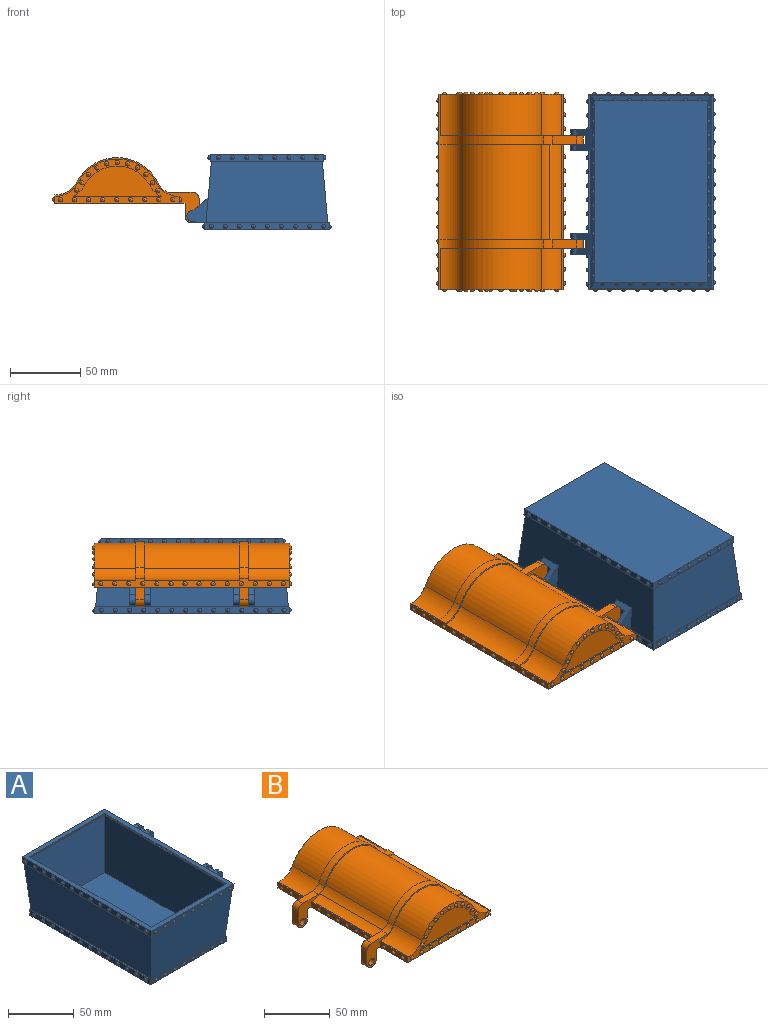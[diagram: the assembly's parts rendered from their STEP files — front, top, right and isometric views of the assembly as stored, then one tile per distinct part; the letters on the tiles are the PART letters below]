
ASSEMBLY  parts=2 mates=1
PART A: 134 faces, bbox 102.8x141.6x54 mm
  f0: plane 15x9.96mm, normal (0.09,0,1), area 101mm2, adj f11,f30,f31,f35,f36,f37,f40,f41
  f1: plane 15x9.96mm, normal (0.09,0,1), area 101mm2, adj f11,f28,f29,f32,f33,f34,f42,f43
  f2: plane 86.7x44mm, normal (0,-1,-0.09), area 3659.3mm2, adj f5,f9,f10,f11
  f3: plane 139x88.7mm, normal (0,0,1), area 1760.1mm2, adj f4,f12,f14,f17,f22,f25,f26,f27
  f4: plane 139x5mm, normal (-1,0,0), area 593.9mm2, adj f3,f11,f14,f17,f76,f77,f78,f79
  f5: plane 137.13x44mm, normal (-1,0,-0.09), area 5886.5mm2, adj f2,f9,f11,f13
  f6: plane 130.43x5mm, normal (-1,0,0), area 558.1mm2, adj f7,f9,f15,f16,f90,f91,f92,f93
  f7: plane 129.55x81mm, normal (0,0,-1), area 10493.6mm2, adj f6,f8,f15,f16
  f8: plane 130.43x5mm, normal (1,0,0), area 558.1mm2, adj f7,f9,f15,f16,f111,f112,f113,f114
  f9: plane 130.43x81mm, normal (0,0,1), area 339.9mm2, adj f2,f5,f6,f8,f10,f13,f15,f16
  f10: plane 137.13x44mm, normal (1,0,-0.09), area 5346.5mm2, adj f2,f9,f11,f13,f28,f29,f30,f31
  f11: plane 138.13x88.7mm, normal (0,0,-1), area 362.9mm2, adj f0,f1,f2,f4,f5,f10,f12,f13
  f12: plane 139x5mm, normal (1,0,0), area 593.9mm2, adj f3,f11,f14,f17,f53,f54,f55,f56
  f13: plane 86.7x44mm, normal (0,1,-0.09), area 3659.3mm2, adj f5,f9,f10,f11
  f14: plane 88.7x5mm, normal (0,-1,-0.09), area 381.6mm2, adj f3,f4,f11,f12,f44,f45,f46,f47
  f15: plane 81x5mm, normal (0,-1,-0.09), area 350mm2, adj f6,f7,f8,f9,f124,f125,f126,f127
  f16: plane 81x5mm, normal (0,1,-0.09), area 350mm2, adj f6,f7,f8,f9,f103,f104,f105,f106
  f17: plane 88.7x5mm, normal (0,1,-0.09), area 381.6mm2, adj f3,f4,f11,f12,f67,f68,f69,f70
  f18: plane 129.79x49mm, normal (1,0,0.09), area 6173.4mm2, adj f19,f21,f23,f24
  f19: plane 79.37x49mm, normal (0,1,0.09), area 3693mm2, adj f18,f20,f23,f24
  f20: plane 129.79x49mm, normal (-1,0,0.09), area 6173.4mm2, adj f19,f21,f23,f24
  f21: plane 79.37x49mm, normal (0,-1,0.09), area 3693mm2, adj f18,f20,f23,f24
  f22: plane 130.97x1mm, normal (1,0,0), area 130.9mm2, adj f3,f24,f26,f27
  f23: plane 121.22x70.79mm, normal (0,0,1), area 8581.7mm2, adj f18,f19,f20,f21
  f24: plane 130.79x80.7mm, normal (0,0,1), area 253.4mm2, adj f18,f19,f20,f21,f22,f25,f26,f27
  f25: plane 130.97x1mm, normal (-1,0,0), area 130.9mm2, adj f3,f24,f26,f27
  f26: plane 80.7x1mm, normal (0,1,0.09), area 81mm2, adj f3,f22,f24,f25
  f27: plane 80.7x1mm, normal (0,-1,0.09), area 81mm2, adj f3,f22,f24,f25
  f28: plane 17.93x15.18mm, normal (0,-1,0), area 155.1mm2, adj f1,f10,f43,f133
  f29: plane 17.93x15.18mm, normal (0,1,0), area 155.1mm2, adj f1,f10,f42,f133
  f30: plane 17.93x15.18mm, normal (0,1,0), area 155.1mm2, adj f0,f10,f40,f132
  f31: plane 17.93x15.18mm, normal (0,-1,0), area 155.1mm2, adj f0,f10,f41,f132
  f32: plane 14.94x11.93mm, normal (0,1,0), area 93.1mm2, adj f1,f34,f38,f43,f133
  f33: plane 14.94x11.93mm, normal (0,-1,0), area 93.1mm2, adj f1,f34,f38,f42,f133
  f34: plane 14.94x7mm, normal (1,0,-0.09), area 105mm2, adj f1,f32,f33,f133
  f35: plane 14.94x11.93mm, normal (0,1,0), area 93.1mm2, adj f0,f37,f39,f41,f132
  f36: plane 14.94x11.93mm, normal (0,-1,0), area 93.1mm2, adj f0,f37,f39,f40,f132
  f37: plane 14.94x7mm, normal (1,0,-0.09), area 105mm2, adj f0,f35,f36,f132
  f38: cylinder r=2mm len=7mm, axis (0,-1,0), area 88mm2, adj f32,f33
  f39: cylinder r=2mm len=7mm, axis (0,1,0), area 88mm2, adj f35,f36
  f40: cylinder r=4mm len=7.98mm, axis (0,-1,0), area 50.3mm2, adj f0,f30,f36,f132
  f41: cylinder r=4mm len=7.98mm, axis (0,1,0), area 50.3mm2, adj f0,f31,f35,f132
  f42: cylinder r=4mm len=7.98mm, axis (0,-1,0), area 50.3mm2, adj f1,f29,f33,f133
  f43: cylinder r=4mm len=7.98mm, axis (0,1,0), area 50.3mm2, adj f1,f28,f32,f133
  f44: sphere r=1.5mm, area 14.1mm2, adj f14
  f45: sphere r=1.5mm, area 14.1mm2, adj f14
  f46: sphere r=1.5mm, area 14.1mm2, adj f14
  f47: sphere r=1.5mm, area 14.1mm2, adj f14
  f48: sphere r=1.5mm, area 14.1mm2, adj f14
  f49: sphere r=1.5mm, area 14.1mm2, adj f14
  f50: sphere r=1.5mm, area 14.1mm2, adj f14
  f51: sphere r=1.5mm, area 14.1mm2, adj f14
  f52: sphere r=1.5mm, area 14.1mm2, adj f14
  f53: sphere r=1.5mm, area 14.1mm2, adj f12
  f54: sphere r=1.5mm, area 14.1mm2, adj f12
  f55: sphere r=1.5mm, area 14.1mm2, adj f12
  f56: sphere r=1.5mm, area 14.1mm2, adj f12
  f57: sphere r=1.5mm, area 14.1mm2, adj f12
  f58: sphere r=1.5mm, area 14.1mm2, adj f12
  f59: sphere r=1.5mm, area 14.1mm2, adj f12
  f60: sphere r=1.5mm, area 14.1mm2, adj f12
  f61: sphere r=1.5mm, area 14.1mm2, adj f12
  f62: sphere r=1.5mm, area 14.1mm2, adj f12
  f63: sphere r=1.5mm, area 14.1mm2, adj f12
  f64: sphere r=1.5mm, area 14.1mm2, adj f12
  f65: sphere r=1.5mm, area 14.1mm2, adj f12
  f66: sphere r=1.5mm, area 14.1mm2, adj f12
  f67: sphere r=1.5mm, area 14.1mm2, adj f17
  f68: sphere r=1.5mm, area 14.1mm2, adj f17
  f69: sphere r=1.5mm, area 14.1mm2, adj f17
  f70: sphere r=1.5mm, area 14.1mm2, adj f17
  f71: sphere r=1.5mm, area 14.1mm2, adj f17
  f72: sphere r=1.5mm, area 14.1mm2, adj f17
  f73: sphere r=1.5mm, area 14.1mm2, adj f17
  f74: sphere r=1.5mm, area 14.1mm2, adj f17
  f75: sphere r=1.5mm, area 14.1mm2, adj f17
  f76: sphere r=1.5mm, area 14.1mm2, adj f4
  f77: sphere r=1.5mm, area 14.1mm2, adj f4
  f78: sphere r=1.5mm, area 14.1mm2, adj f4
  f79: sphere r=1.5mm, area 14.1mm2, adj f4
  f80: sphere r=1.5mm, area 14.1mm2, adj f4
  f81: sphere r=1.5mm, area 14.1mm2, adj f4
  f82: sphere r=1.5mm, area 14.1mm2, adj f4
  f83: sphere r=1.5mm, area 14.1mm2, adj f4
  f84: sphere r=1.5mm, area 14.1mm2, adj f4
  f85: sphere r=1.5mm, area 14.1mm2, adj f4
  f86: sphere r=1.5mm, area 14.1mm2, adj f4
  f87: sphere r=1.5mm, area 14.1mm2, adj f4
  f88: sphere r=1.5mm, area 14.1mm2, adj f4
  f89: sphere r=1.5mm, area 14.1mm2, adj f4
  f90: sphere r=1.5mm, area 14.1mm2, adj f6
  f91: sphere r=1.5mm, area 14.1mm2, adj f6
  f92: sphere r=1.5mm, area 14.1mm2, adj f6
  f93: sphere r=1.5mm, area 14.1mm2, adj f6
  f94: sphere r=1.5mm, area 14.1mm2, adj f6
  f95: sphere r=1.5mm, area 14.1mm2, adj f6
  f96: sphere r=1.5mm, area 14.1mm2, adj f6
  f97: sphere r=1.5mm, area 14.1mm2, adj f6
  f98: sphere r=1.5mm, area 14.1mm2, adj f6
  f99: sphere r=1.5mm, area 14.1mm2, adj f6
  f100: sphere r=1.5mm, area 14.1mm2, adj f6
  f101: sphere r=1.5mm, area 14.1mm2, adj f6
  f102: sphere r=1.5mm, area 14.1mm2, adj f6
  f103: sphere r=1.5mm, area 14.1mm2, adj f16
  f104: sphere r=1.5mm, area 14.1mm2, adj f16
  f105: sphere r=1.5mm, area 14.1mm2, adj f16
  f106: sphere r=1.5mm, area 14.1mm2, adj f16
  f107: sphere r=1.5mm, area 14.1mm2, adj f16
  f108: sphere r=1.5mm, area 14.1mm2, adj f16
  f109: sphere r=1.5mm, area 14.1mm2, adj f16
  f110: sphere r=1.5mm, area 14.1mm2, adj f16
  f111: sphere r=1.5mm, area 14.1mm2, adj f8
  f112: sphere r=1.5mm, area 14.1mm2, adj f8
  f113: sphere r=1.5mm, area 14.1mm2, adj f8
  f114: sphere r=1.5mm, area 14.1mm2, adj f8
  f115: sphere r=1.5mm, area 14.1mm2, adj f8
  f116: sphere r=1.5mm, area 14.1mm2, adj f8
  f117: sphere r=1.5mm, area 14.1mm2, adj f8
  f118: sphere r=1.5mm, area 14.1mm2, adj f8
  f119: sphere r=1.5mm, area 14.1mm2, adj f8
  f120: sphere r=1.5mm, area 14.1mm2, adj f8
  f121: sphere r=1.5mm, area 14.1mm2, adj f8
  f122: sphere r=1.5mm, area 14.1mm2, adj f8
  f123: sphere r=1.5mm, area 14.1mm2, adj f8
  f124: sphere r=1.5mm, area 14.1mm2, adj f15
  f125: sphere r=1.5mm, area 14.1mm2, adj f15
  f126: sphere r=1.5mm, area 14.1mm2, adj f15
  f127: sphere r=1.5mm, area 14.1mm2, adj f15
  f128: sphere r=1.5mm, area 14.1mm2, adj f15
  f129: sphere r=1.5mm, area 14.1mm2, adj f15
  f130: sphere r=1.5mm, area 14.1mm2, adj f15
  f131: sphere r=1.5mm, area 14.1mm2, adj f15
  f132: plane 15x10.83mm, normal (0.64,0,-0.77), area 142.8mm2, adj f10,f30,f31,f35,f36,f37,f40,f41
  f133: plane 15x10.83mm, normal (0.64,0,-0.77), area 142.8mm2, adj f10,f28,f29,f32,f33,f34,f42,f43
PART B: 141 faces, bbox 104.2x142x46.5 mm
  f0: plane 139x6.1mm, normal (1,0,0), area 609.2mm2, adj f3,f4,f9,f11,f13,f14,f15,f22
  f1: cylinder r=10.19mm len=6.35mm, axis (0,1,0), area 47.9mm2, adj f2,f9,f10,f38
  f2: cylinder r=32.5mm len=59.23mm, axis (0,1,0), area 447.4mm2, adj f1,f3,f9,f38
  f3: cylinder r=16.38mm len=15.12mm, axis (0,1,0), area 108.3mm2, adj f0,f2,f9,f38
  f4: plane 29.5x1mm, normal (0,0,1), area 29.5mm2, adj f0,f5,f13,f38
  f5: cylinder r=17.43mm len=29.5mm, axis (0,1,0), area 513.7mm2, adj f4,f6,f13,f38
  f6: cylinder r=31.5mm len=57.38mm, axis (0,1,0), area 2128.7mm2, adj f5,f8,f13,f38
  f7: cylinder r=17.43mm len=68mm, axis (0,1,0), area 627mm2, adj f9,f11,f19,f138
  f8: cylinder r=17.43mm len=29.5mm, axis (0,1,0), area 513.7mm2, adj f6,f13,f26,f38
  f9: plane 102.71x46.51mm, normal (0,-1,0), area 329.8mm2, adj f0,f1,f2,f3,f7,f10,f15,f19
  f10: plane 17x6mm, normal (0,0,1), area 102mm2, adj f1,f9,f38,f51
  f11: plane 102.71x46.51mm, normal (0,1,0), area 329.8mm2, adj f0,f7,f12,f15,f19,f20,f44,f46
  f12: plane 17x6mm, normal (0,0,1), area 102mm2, adj f11,f43,f52,f131
  f13: plane 88.7x31.5mm, normal (0,1,0), area 730.5mm2, adj f0,f4,f5,f6,f8,f15,f26,f27
  f14: plane 88.7x31.5mm, normal (0,-1,0), area 730.7mm2, adj f0,f15,f16,f17,f22,f23,f24,f25
  f15: plane 139x92.7mm, normal (0,0,-1), area 1865.6mm2, adj f0,f9,f11,f13,f14,f17,f18,f20
  f16: plane 29.5x1mm, normal (0,0,1), area 29.5mm2, adj f14,f17,f25,f43
  f17: plane 29.5x5mm, normal (-1,0,0), area 126.3mm2, adj f14,f15,f16,f43,f108,f109,f110
  f18: plane 25.5x1.21mm, normal (1,0,0), area 30.9mm2, adj f15,f30,f33,f41
  f19: plane 68x1mm, normal (0,0,1), area 68mm2, adj f7,f9,f11,f20
  f20: plane 68x5mm, normal (-1,0,0), area 297.6mm2, adj f9,f11,f15,f19,f111,f112,f113,f114
  f21: plane 68x1.21mm, normal (1,0,0), area 82.4mm2, adj f15,f30,f35,f42
  f22: plane 29.5x1mm, normal (0,0,1), area 29.5mm2, adj f0,f14,f23,f43
  f23: cylinder r=17.43mm len=29.5mm, axis (0,1,0), area 513.7mm2, adj f14,f22,f24,f43
  f24: cylinder r=31.5mm len=57.38mm, axis (0,1,0), area 2128.7mm2, adj f14,f23,f25,f43
  f25: cylinder r=17.43mm len=29.5mm, axis (0,1,0), area 513.7mm2, adj f14,f16,f24,f43
  f26: plane 29.5x1mm, normal (0,0,1), area 29.5mm2, adj f8,f13,f27,f38
  f27: plane 29.5x5mm, normal (-1,0,0), area 126.3mm2, adj f13,f15,f26,f38,f105,f106,f107
  f28: cylinder r=21.43mm len=131mm, axis (0,1,0), area 2394.2mm2, adj f29,f32,f33,f34,f134,f135,f136,f137
  f29: cylinder r=27.5mm len=131mm, axis (0,1,0), area 8322.6mm2, adj f28,f30,f33,f34
  f30: cylinder r=21.43mm len=131mm, axis (0,1,0), area 2320.7mm2, adj f18,f21,f29,f31,f33,f34,f35,f36
  f31: plane 25.5x1.21mm, normal (1,0,0), area 30.9mm2, adj f15,f30,f34,f36
  f32: plane 131x1.21mm, normal (-1,0,0), area 158.6mm2, adj f15,f28,f33,f34
  f33: plane 80.7x27.5mm, normal (0,1,0), area 1290.9mm2, adj f15,f18,f28,f29,f30,f32
  f34: plane 80.7x27.5mm, normal (0,-1,0), area 1290.9mm2, adj f15,f28,f29,f30,f31,f32
  f35: plane 10x5.39mm, normal (0,-1,0), area 22.6mm2, adj f15,f21,f30,f37,f64
  f36: plane 10x5.39mm, normal (0,1,0), area 22.6mm2, adj f15,f30,f31,f37,f64
  f37: plane 6x0.39mm, normal (1,0,0), area 2.4mm2, adj f30,f35,f36,f64
  f38: plane 102.7x46.5mm, normal (0,1,0), area 329.5mm2, adj f0,f1,f2,f3,f4,f5,f6,f8
  f39: plane 12x6mm, normal (-1,0,0), area 72mm2, adj f9,f38,f50,f51
  f40: plane 6x0.39mm, normal (1,0,0), area 2.4mm2, adj f30,f41,f42,f63
  f41: plane 10x5.39mm, normal (0,-1,0), area 22.6mm2, adj f15,f18,f30,f40,f63
  f42: plane 10x5.39mm, normal (0,1,0), area 22.6mm2, adj f15,f21,f30,f40,f63
  f43: plane 102.7x46.5mm, normal (0,-1,0), area 329.5mm2, adj f0,f12,f15,f16,f17,f22,f23,f24
  f44: plane 12x6mm, normal (-1,0,0), area 72mm2, adj f11,f43,f49,f52
  f45: plane 9x6mm, normal (1,0,0), area 54mm2, adj f9,f15,f38,f50
  f46: plane 9x6mm, normal (1,0,0), area 54mm2, adj f11,f15,f43,f49
  f47: cylinder r=3mm len=6mm, axis (0,1,0), area 113.1mm2, adj f11,f43
  f48: cylinder r=3mm len=6mm, axis (0,1,0), area 113.1mm2, adj f9,f38
  f49: cylinder r=5mm len=10mm, axis (0,1,0), area 94.2mm2, adj f11,f43,f44,f46
  f50: cylinder r=5mm len=10mm, axis (0,1,0), area 94.2mm2, adj f9,f38,f39,f45
  f51: cylinder r=5mm len=6mm, axis (0,-1,0), area 47.1mm2, adj f9,f10,f38,f39
  f52: cylinder r=5mm len=6mm, axis (0,-1,0), area 47.1mm2, adj f11,f12,f43,f44
  f53: cylinder r=26.5mm len=47.27mm, axis (0,-1,0), area 58.4mm2, adj f14,f54,f56,f57
  f54: cylinder r=17.43mm len=7.72mm, axis (0,-1,0), area 10.6mm2, adj f14,f53,f55,f57
  f55: plane 62.7x1mm, normal (0,0,1), area 62.7mm2, adj f14,f54,f56,f57
  f56: cylinder r=17.43mm len=7.72mm, axis (0,-1,0), area 10.6mm2, adj f14,f53,f55,f57
  f57: plane 62.7x21.5mm, normal (0,-1,0), area 863.2mm2, adj f53,f54,f55,f56
  f58: cylinder r=26.5mm len=46.87mm, axis (0,1,0), area 57.5mm2, adj f13,f59,f61,f62
  f59: cylinder r=17.43mm len=7.91mm, axis (0,1,0), area 11mm2, adj f13,f58,f60,f62
  f60: plane 62.7x1mm, normal (0,0,1), area 62.7mm2, adj f13,f59,f61,f62
  f61: cylinder r=17.43mm len=7.91mm, axis (0,1,0), area 11mm2, adj f13,f58,f60,f62
  f62: plane 62.7x21.5mm, normal (0,1,0), area 863.4mm2, adj f58,f59,f60,f61
  f63: cylinder r=5mm len=6mm, axis (0,1,0), area 47.1mm2, adj f15,f40,f41,f42
  f64: cylinder r=5mm len=6mm, axis (0,1,0), area 47.1mm2, adj f15,f35,f36,f37
  f65: sphere r=1.5mm, area 14.1mm2, adj f13
  f66: sphere r=1.5mm, area 14.1mm2, adj f13
  f67: sphere r=1.5mm, area 14.1mm2, adj f13
  f68: sphere r=1.5mm, area 14.1mm2, adj f13
  f69: sphere r=1.5mm, area 14.1mm2, adj f13
  f70: sphere r=1.5mm, area 14.1mm2, adj f13
  f71: sphere r=1.5mm, area 14.1mm2, adj f13
  f72: sphere r=1.5mm, area 14.1mm2, adj f13
  f73: sphere r=1.5mm, area 14.1mm2, adj f13
  f74: sphere r=1.5mm, area 14.1mm2, adj f13
  f75: sphere r=1.5mm, area 14.1mm2, adj f13
  f76: sphere r=1.5mm, area 14.1mm2, adj f13
  f77: sphere r=1.5mm, area 14.1mm2, adj f13
  f78: sphere r=1.5mm, area 14.1mm2, adj f13
  f79: sphere r=1.5mm, area 14.1mm2, adj f13
  f80: sphere r=1.5mm, area 14.1mm2, adj f13
  f81: sphere r=1.5mm, area 14.1mm2, adj f13
  f82: sphere r=1.5mm, area 14.1mm2, adj f13
  f83: sphere r=1.5mm, area 14.1mm2, adj f13
  f84: sphere r=1.5mm, area 14.1mm2, adj f13
  f85: sphere r=1.5mm, area 14.1mm2, adj f14
  f86: sphere r=1.5mm, area 14.1mm2, adj f14
  f87: sphere r=1.5mm, area 14.1mm2, adj f14
  f88: sphere r=1.5mm, area 14.1mm2, adj f14
  f89: sphere r=1.5mm, area 14.1mm2, adj f14
  f90: sphere r=1.5mm, area 14.1mm2, adj f14
  f91: sphere r=1.5mm, area 14.1mm2, adj f14
  f92: sphere r=1.5mm, area 14.1mm2, adj f14
  f93: sphere r=1.5mm, area 14.1mm2, adj f14
  f94: sphere r=1.5mm, area 14.1mm2, adj f14
  f95: sphere r=1.5mm, area 14.1mm2, adj f14
  f96: sphere r=1.5mm, area 14.1mm2, adj f14
  f97: sphere r=1.5mm, area 14.1mm2, adj f14
  f98: sphere r=1.5mm, area 14.1mm2, adj f14
  f99: sphere r=1.5mm, area 14.1mm2, adj f14
  f100: sphere r=1.5mm, area 14.1mm2, adj f14
  f101: sphere r=1.5mm, area 14.1mm2, adj f14
  f102: sphere r=1.5mm, area 14.1mm2, adj f14
  f103: sphere r=1.5mm, area 14.1mm2, adj f14
  f104: sphere r=1.5mm, area 14.1mm2, adj f14
  f105: sphere r=1.5mm, area 14.1mm2, adj f27
  f106: sphere r=1.5mm, area 14.1mm2, adj f27
  f107: sphere r=1.5mm, area 14.1mm2, adj f27
  f108: sphere r=1.5mm, area 14.1mm2, adj f17
  f109: sphere r=1.5mm, area 14.1mm2, adj f17
  f110: sphere r=1.5mm, area 14.1mm2, adj f17
  f111: sphere r=1.5mm, area 14.1mm2, adj f20
  f112: sphere r=1.5mm, area 14.1mm2, adj f20
  f113: sphere r=1.5mm, area 14.1mm2, adj f20
  f114: sphere r=1.5mm, area 14.1mm2, adj f20
  f115: sphere r=1.5mm, area 14.1mm2, adj f20
  f116: sphere r=1.5mm, area 14.1mm2, adj f20
  f117: sphere r=1.5mm, area 14.1mm2, adj f0
  f118: sphere r=1.5mm, area 14.1mm2, adj f0
  f119: sphere r=1.5mm, area 14.1mm2, adj f0
  f120: sphere r=1.5mm, area 14.1mm2, adj f0
  f121: sphere r=1.5mm, area 14.1mm2, adj f0
  f122: sphere r=1.5mm, area 14.1mm2, adj f0
  f123: sphere r=1.5mm, area 14.1mm2, adj f0
  f124: sphere r=1.5mm, area 14.1mm2, adj f0
  f125: sphere r=1.5mm, area 14.1mm2, adj f0
  f126: sphere r=1.5mm, area 14.1mm2, adj f0
  f127: sphere r=1.5mm, area 14.1mm2, adj f0
  f128: sphere r=1.5mm, area 14.1mm2, adj f0
  f129: sphere r=1.5mm, area 14.1mm2, adj f0
  f130: sphere r=1.5mm, area 14.1mm2, adj f0
  f131: cylinder r=10.19mm len=6.35mm, axis (0,1,0), area 47.9mm2, adj f11,f12,f43,f132
  f132: cylinder r=32.5mm len=59.23mm, axis (0,1,0), area 447.4mm2, adj f11,f43,f131,f133
  f133: cylinder r=16.38mm len=15.12mm, axis (0,1,0), area 108.3mm2, adj f0,f11,f43,f132
  f134: cylinder r=31mm len=80mm, axis (0,1,0), area 34.3mm2, adj f28,f135,f136,f137
  f135: plane 80x0.52mm, normal (0,0,-1), area 41.5mm2, adj f28,f134,f136,f137
  f136: plane 0.59x0.42mm, normal (0,-1,0), area 0.1mm2, adj f28,f134,f135
  f137: plane 0.59x0.42mm, normal (0,1,0), area 0.1mm2, adj f28,f134,f135
  f138: cylinder r=17.43mm len=68mm, axis (0,-1,0), area 557.7mm2, adj f7,f9,f11,f139
  f139: cylinder r=31.5mm len=68mm, axis (0,-1,0), area 4906.2mm2, adj f9,f11,f138,f140
  f140: cylinder r=17.43mm len=68mm, axis (0,-1,0), area 1253.2mm2, adj f0,f9,f11,f139
PLACE A rot(axis=(0,1,0),180deg) t=(28.27,20.06,18.24)mm
PLACE B rot(axis=(0,0,1),180deg) t=(-117.88,-118.44,-16.77)mm
MATE cylindrical B.f47 <-> A.f38  axis (0,-1,0) through (-64.53,-85.94,-26.07)mm
